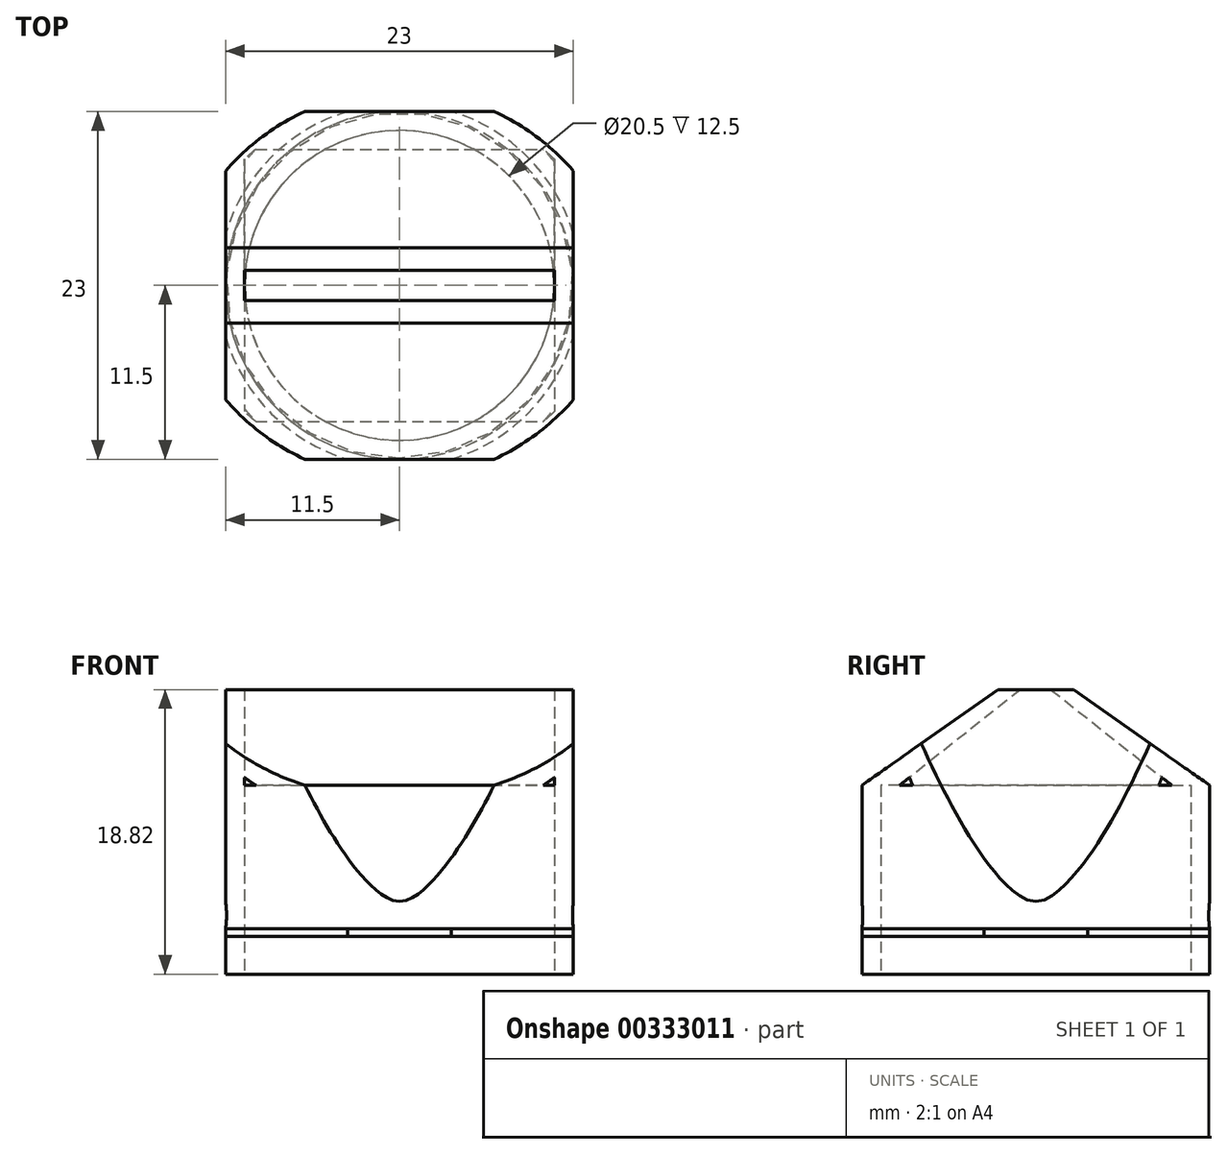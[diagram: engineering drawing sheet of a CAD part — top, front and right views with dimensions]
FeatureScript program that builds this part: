
annotation { "Feature Type Name" : "Feature", "Feature Type Description" : "" }
export const myFeature = defineFeature(function(context is Context, id is Id, definition is map)
    precondition{}
    {
        {
            var Q0;
            Q0=qCreatedBy(makeId("Top.planeOp"),FACE);
            var sketch = newSketch(context, id + "F0", { "sketchPlane" : qUnion([Q0])});
            skCircle(sketch, "E0", {"center": v(0, 0) * mm, "radius": 10.25 * mm});
            skSolve(sketch);
        }
        {
            var Q0;
            Q0=qCreatedBy(makeId("Top.planeOp"),FACE);
            var sketch = newSketch(context, id + "F1", { "sketchPlane" : qUnion([Q0])});
            skLineSegment(sketch, "E1.bottom", {"start": v(11.5, 11.5) * mm, "end": v(-11.5, 11.5) * mm});
            skLineSegment(sketch, "E1.top", {"start": v(11.5, -11.5) * mm, "end": v(-11.5, -11.5) * mm});
            skLineSegment(sketch, "E1.left", {"start": v(11.5, 11.5) * mm, "end": v(11.5, -11.5) * mm});
            skLineSegment(sketch, "E1.right", {"start": v(-11.5, 11.5) * mm, "end": v(-11.5, -11.5) * mm});
            skPoint(sketch, "E1.middle", {"position": v(0, 0) * mm});
            skSolve(sketch);
        }
        {
            var Q0;
            Q0 = qSketchRegion(id + "F1", true);
            extrude(context, id + "F2", {"entities" : qUnion([Q0]), "depth" : 30 * mm});
        }
        {
            var Q0;
            Q0 = qSketchRegion(id + "F0", true);
            extrude(context, id + "F3", {"entities" : qUnion([Q0]), "operationType" : NewBodyOperationType.REMOVE, "oppositeDirection" : true, "depth" : -12.5 * mm});
        }
        {
            var Q0;
            Q0=qCreatedBy(makeId("Right.planeOp"),FACE);
            var sketch = newSketch(context, id + "F4", { "sketchPlane" : qUnion([Q0])});
            skLineSegment(sketch, "E2", {"start": v(0, 0) * mm, "end": v(0, 27.08) * mm});
            skSolve(sketch);
        }
        {
            var Q0;
            Q0=qCreatedBy(makeId("Right.planeOp"),FACE);
            var sketch = newSketch(context, id + "F5", { "sketchPlane" : qUnion([Q0])});
            skLineSegment(sketch, "E3", {"start": v(-35.58, 20) * mm, "end": v(-35.58, 0) * mm});
            skLineSegment(sketch, "E4", {"start": v(-11.5, 0) * mm, "end": v(-11.5, 2.5) * mm});
            skLineSegment(sketch, "E5", {"start": v(-11.5, 2.5) * mm, "end": v(-11.5, 0) * mm});
            skLineSegment(sketch, "E6", {"start": v(-35.58, 0) * mm, "end": v(-11.5, 0) * mm});
            skLineSegment(sketch, "E7", {"start": v(-11.5, 2.5) * mm, "end": v(-12, 2.5) * mm});
            skLineSegment(sketch, "E8", {"start": v(-12, 2.5) * mm, "end": v(-12, 3) * mm});
            skLineSegment(sketch, "E9", {"start": v(-12, 3) * mm, "end": v(-11.5, 3) * mm});
            skPoint(sketch, "E10.1.internal.orphan", {"position": v(-11.5, 4.8) * mm});
            skLineSegment(sketch, "E11", {"start": v(-35.58, 20) * mm, "end": v(-14.95, 20) * mm});
            skFitSpline(sketch, "E12", {"points": [v(-11.5, 3) * mm, v(-11.5, 4.8) * mm, v(-14.95, 20) * mm], "startDerivative": vector(0.59, 5.42) * mm, "endDerivative": vector(-6.35, 25.31) * mm});
            skFitSpline(sketch, "E13", {"points": [v(-14.95, 20) * mm, v(-14.95, 11.77) * mm, v(-11.5, 4.8) * mm, v(-11.45, 3.46) * mm], "startDerivative": vector(-3.14, -19.36) * mm, "endDerivative": vector(-1.35, -6.54) * mm});
            skSolve(sketch);
        }
        {
            var Q0;
            Q0=qCreatedBy(makeId("Right.planeOp"),FACE);
            var sketch = newSketch(context, id + "F6", { "sketchPlane" : qUnion([Q0])});
            skLineSegment(sketch, "E14", {"start": v(0, 0) * mm, "end": v(0, 12.5) * mm});
            skLineSegment(sketch, "E15", {"start": v(0, 12.5) * mm, "end": v(11.5, 12.5) * mm});
            skLineSegment(sketch, "E16", {"start": v(11.5, 12.5) * mm, "end": v(-11.5, 12.5) * mm});
            skLineSegment(sketch, "E17", {"start": v(-11.5, 12.5) * mm, "end": v(-2.5, 18.82) * mm});
            skLineSegment(sketch, "E18", {"start": v(-2.5, 18.82) * mm, "end": v(0, 18.82) * mm});
            skLineSegment(sketch, "E19", {"start": v(0, 18.82) * mm, "end": v(2.5, 18.82) * mm});
            skLineSegment(sketch, "E20", {"start": v(2.5, 18.82) * mm, "end": v(11.5, 12.5) * mm});
            skSolve(sketch);
        }
        {
            var Q0;
            Q0 = qSketchRegion(id + "F6", true);
            extrude(context, id + "F7", {"entities" : qUnion([Q0]), "operationType" : NewBodyOperationType.ADD, "endBound" : BoundingType.SYMMETRIC, "depth" : 23 * mm});
        }
        {
            var Q0;
            Q0=qCreatedBy(makeId("Right.planeOp"),FACE);
            var sketch = newSketch(context, id + "F8", { "sketchPlane" : qUnion([Q0])});
            skLineSegment(sketch, "E21", {"start": v(0, 0) * mm, "end": v(0, 12.5) * mm});
            skLineSegment(sketch, "E22", {"start": v(0, 18.83) * mm, "end": v(-1, 18.83) * mm});
            skLineSegment(sketch, "E23", {"start": v(-1, 18.83) * mm, "end": v(0, 18.83) * mm});
            skLineSegment(sketch, "E24", {"start": v(1, 18.83) * mm, "end": v(0, 18.83) * mm});
            skLineSegment(sketch, "E25", {"start": v(0, 12.5) * mm, "end": v(-9, 12.5) * mm});
            skLineSegment(sketch, "E26", {"start": v(-9, 12.5) * mm, "end": v(0, 12.5) * mm});
            skLineSegment(sketch, "E27", {"start": v(0, 12.5) * mm, "end": v(9, 12.5) * mm});
            skLineSegment(sketch, "E28", {"start": v(1, 18.83) * mm, "end": v(9, 12.5) * mm});
            skLineSegment(sketch, "E29", {"start": v(-1, 18.83) * mm, "end": v(-9, 12.5) * mm});
            skSolve(sketch);
        }
        {
            var Q0;
            Q0 = qSketchRegion(id + "F8", true);
            extrude(context, id + "F9", {"entities" : qUnion([Q0]), "operationType" : NewBodyOperationType.REMOVE, "endBound" : BoundingType.SYMMETRIC, "oppositeDirection" : true, "depth" : 20.5 * mm});
        }
        {
            var Q0;
            Q0 = qSketchRegion(id + "F5", true);
            var Q1;
            Q1=sQuery(id+"F4.wireOp",EDGE,"E2");
            revolve(context, id + "F10", {"operationType" : NewBodyOperationType.REMOVE, "entities" : qUnion([Q0]), "axis" : qUnion([Q1]), "revolveType" : RevolveType.FULL, "oppositeDirection" : true});
        }
        {
            var Q0;
            Q0=qCreatedBy(makeId("Right.planeOp"),FACE);
            var sketch = newSketch(context, id + "F11", { "sketchPlane" : qUnion([Q0])});
            skLineSegment(sketch, "E30", {"start": v(-11.5, 12.5) * mm, "end": v(-2.5, 18.82) * mm});
            skLineSegment(sketch, "E31", {"start": v(-2.5, 18.82) * mm, "end": v(0, 18.82) * mm});
            skLineSegment(sketch, "E32", {"start": v(0, 18.82) * mm, "end": v(2.5, 18.82) * mm});
            skLineSegment(sketch, "E33", {"start": v(2.5, 18.82) * mm, "end": v(11.5, 12.5) * mm});
            skPoint(sketch, "E34.start.orphan", {"position": v(0, 0) * mm});
            skLineSegment(sketch, "E35", {"start": v(-11.5, 12.5) * mm, "end": v(-11.5, 44.77) * mm});
            skLineSegment(sketch, "E36", {"start": v(-11.5, 44.77) * mm, "end": v(11.5, 44.77) * mm});
            skLineSegment(sketch, "E37", {"start": v(11.5, 44.77) * mm, "end": v(11.5, 12.5) * mm});
            skSolve(sketch);
        }
        {
            var Q0;
            Q0 = qSketchRegion(id + "F11", true);
            extrude(context, id + "F12", {"entities" : qUnion([Q0]), "operationType" : NewBodyOperationType.REMOVE, "endBound" : BoundingType.SYMMETRIC, "oppositeDirection" : true, "depth" : 25 * mm});
        }
    });
